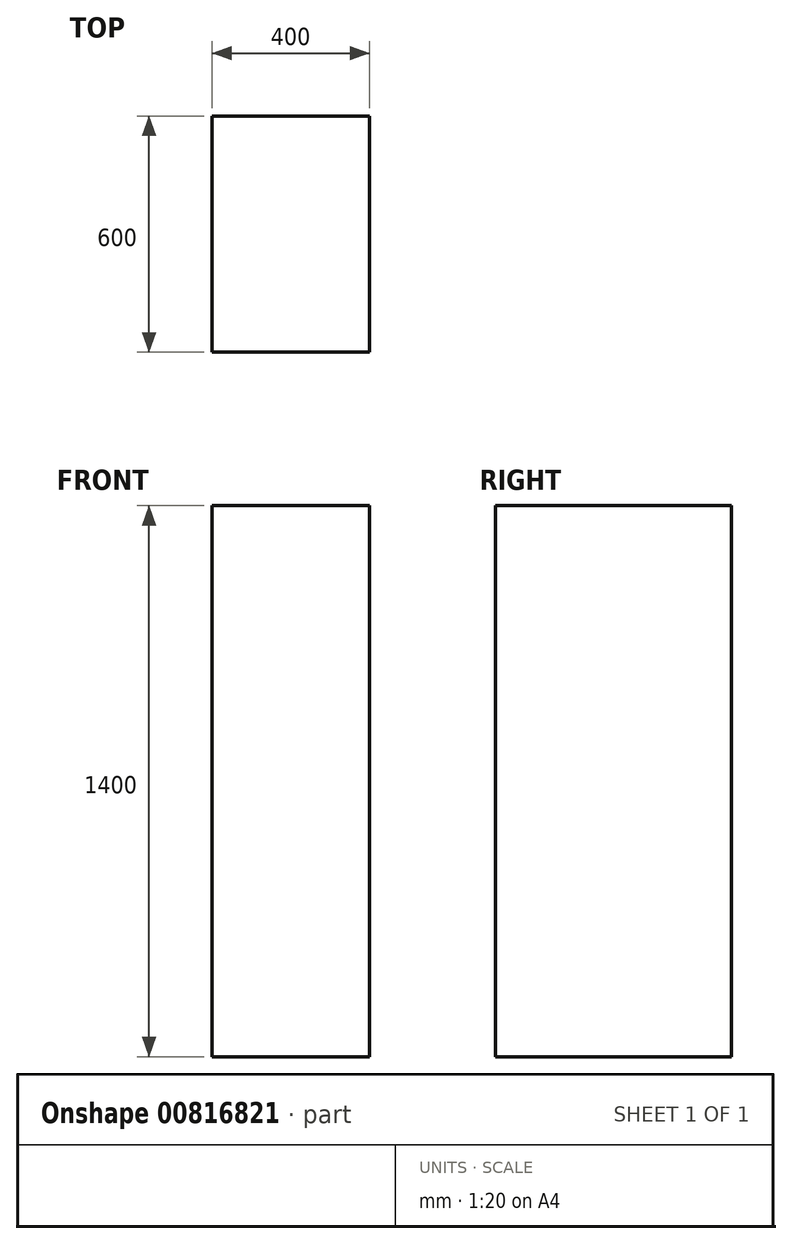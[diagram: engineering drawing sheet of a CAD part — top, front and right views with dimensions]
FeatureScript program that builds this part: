
annotation { "Feature Type Name" : "Feature", "Feature Type Description" : "" }
export const myFeature = defineFeature(function(context is Context, id is Id, definition is map)
    precondition{}
    {
        {
            var Q0;
            Q0=qCreatedBy(makeId("Front.planeOp"),FACE);
            var sketch = newSketch(context, id + "F0", { "sketchPlane" : qUnion([Q0])});
            skLineSegment(sketch, "E0.bottom", {"start": v(0, 0) * mm, "end": v(-400, 0) * mm});
            skLineSegment(sketch, "E0.top", {"start": v(0, 1400) * mm, "end": v(-400, 1400) * mm});
            skLineSegment(sketch, "E0.left", {"start": v(0, 0) * mm, "end": v(0, 1400) * mm});
            skLineSegment(sketch, "E0.right", {"start": v(-400, 0) * mm, "end": v(-400, 1400) * mm});
            skSolve(sketch);
        }
        {
            var Q0;
            Q0=makeQuery(id+"F0.imprint","IMPRINT",FACE,{"disambiguationData":[TD([[makeQuery(id+"F0.imprint","IMPRINT",EDGE,{"derivedFrom":sQuery(id+"F0.wireOp",EDGE,"E0.bottom")}),-1.0]])]});
            extrude(context, id + "F1", {"entities" : qUnion([Q0]), "depth" : 600 * mm, "offsetDistance" : 25 * mm});
        }
    });
